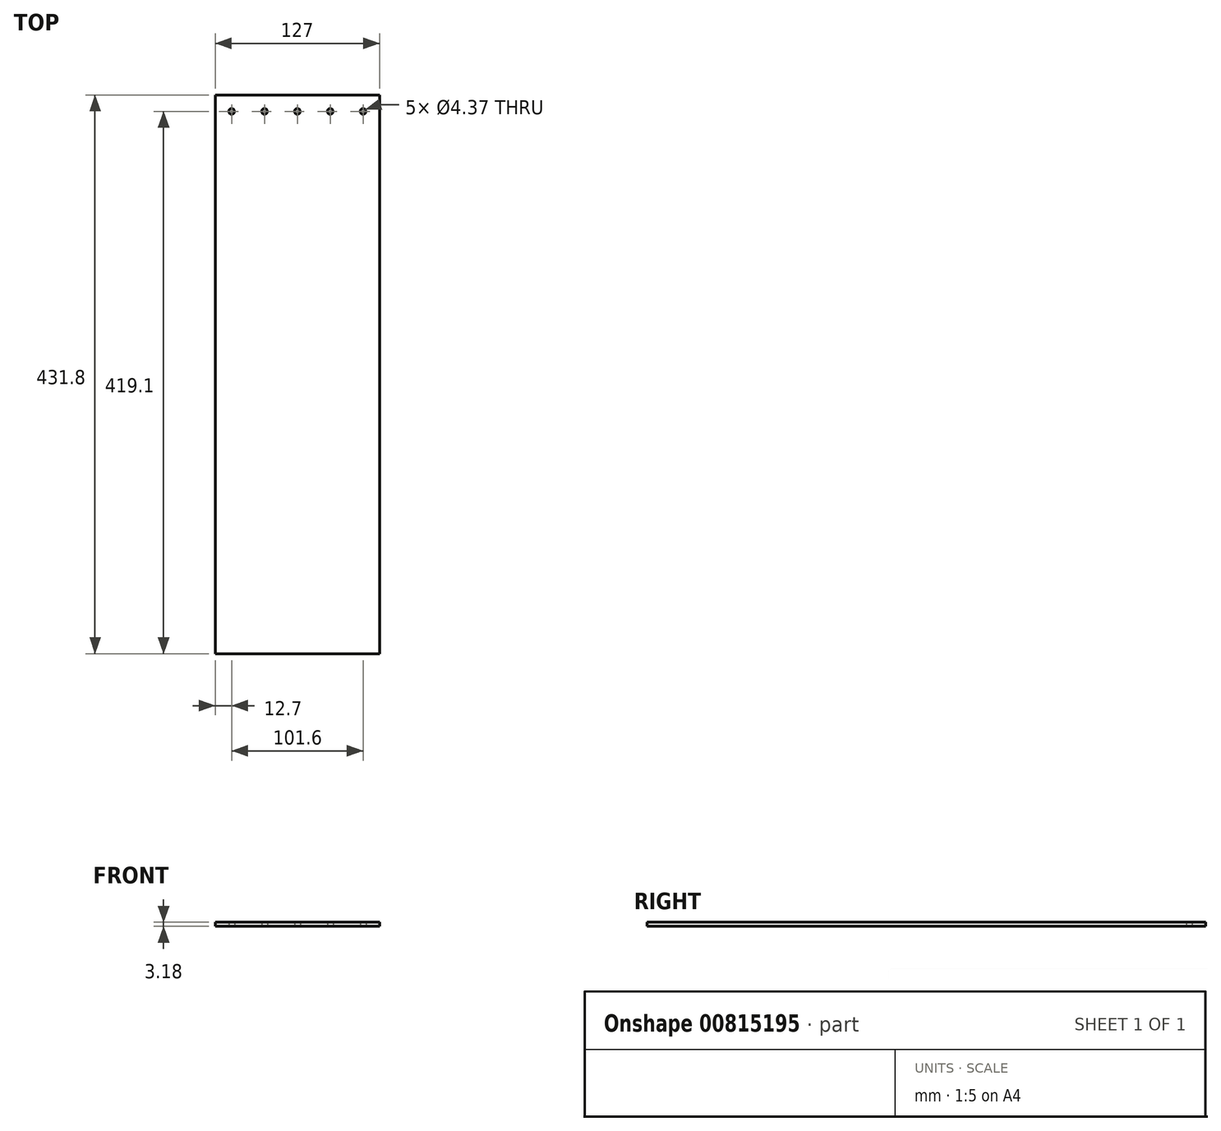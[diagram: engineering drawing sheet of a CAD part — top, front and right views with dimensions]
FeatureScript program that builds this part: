
annotation { "Feature Type Name" : "Feature", "Feature Type Description" : "" }
export const myFeature = defineFeature(function(context is Context, id is Id, definition is map)
    precondition{}
    {
        {
            var Q0;
            Q0=qCreatedBy(makeId("Top.planeOp"),FACE);
            var sketch = newSketch(context, id + "F0", { "sketchPlane" : qUnion([Q0])});
            skLineSegment(sketch, "E0.bottom", {"start": v(0, 0) * mm, "end": v(127, 0) * mm});
            skLineSegment(sketch, "E0.top", {"start": v(0, -431.8) * mm, "end": v(127, -431.8) * mm});
            skLineSegment(sketch, "E0.left", {"start": v(0, 0) * mm, "end": v(0, -431.8) * mm});
            skLineSegment(sketch, "E0.right", {"start": v(127, 0) * mm, "end": v(127, -431.8) * mm});
            skCircle(sketch, "E1", {"center": v(12.7, -12.7) * mm, "radius": 2.18 * mm});
            skCircle(sketch, "E2.1.0.0", {"center": v(38.1, -12.7) * mm, "radius": 2.18 * mm});
            skCircle(sketch, "E2.2.0.0", {"center": v(63.5, -12.7) * mm, "radius": 2.18 * mm});
            skCircle(sketch, "E2.3.0.0", {"center": v(88.9, -12.7) * mm, "radius": 2.18 * mm});
            skCircle(sketch, "E2.4.0.0", {"center": v(114.3, -12.7) * mm, "radius": 2.18 * mm});
            skLineSegment(sketch, "E2.direction1", {"start": v(12.7, -12.7) * mm, "end": v(38.1, -12.7) * mm, "construction": true});
            skSolve(sketch);
        }
        {
            var Q0;
            Q0=makeQuery(id+"F0.imprint","IMPRINT",FACE,{"disambiguationData":[TD([[makeQuery(id+"F0.imprint","IMPRINT",EDGE,{"derivedFrom":sQuery(id+"F0.wireOp",EDGE,"E0.bottom")}),-1.0]])]});
            extrude(context, id + "F1", {"entities" : qUnion([Q0]), "depth" : 3.17 * mm, "offsetDistance" : 25.4 * mm});
        }
    });
